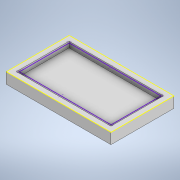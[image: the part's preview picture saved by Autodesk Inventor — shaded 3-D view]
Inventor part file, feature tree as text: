
AUTODESK INVENTOR PART (.ipt)
format: ipt  version: 2021 (Build 250183000, 183)  size: 106,496 bytes
history: native  units: mm
features: sketch x2, extrude x1, shell x1, projected_geometry x1
ambient origin geometry x8: Origin, YZ Plane, XZ Plane, XY Plane, X Axis, Y Axis, Z Axis, Center Point
bodies: Solid1 (feature_tree)
feature tree (5):
  extrude  "Extrusion1"  Depth=1.0mm
  sketch  "Sketch2"
  shell  "Shell1"  [1 undecoded]
  sketch  "Sketch1"  dims[d0=12.25mm d1=0.0mm d2=1.0mm]
  projected_geometry  "Projected Loop1"
note: 1 required parameter value undecoded (feature->parameter linkage not recoverable at this tier; creation-order binding heuristic only, values carry confidence <= 0.55)
